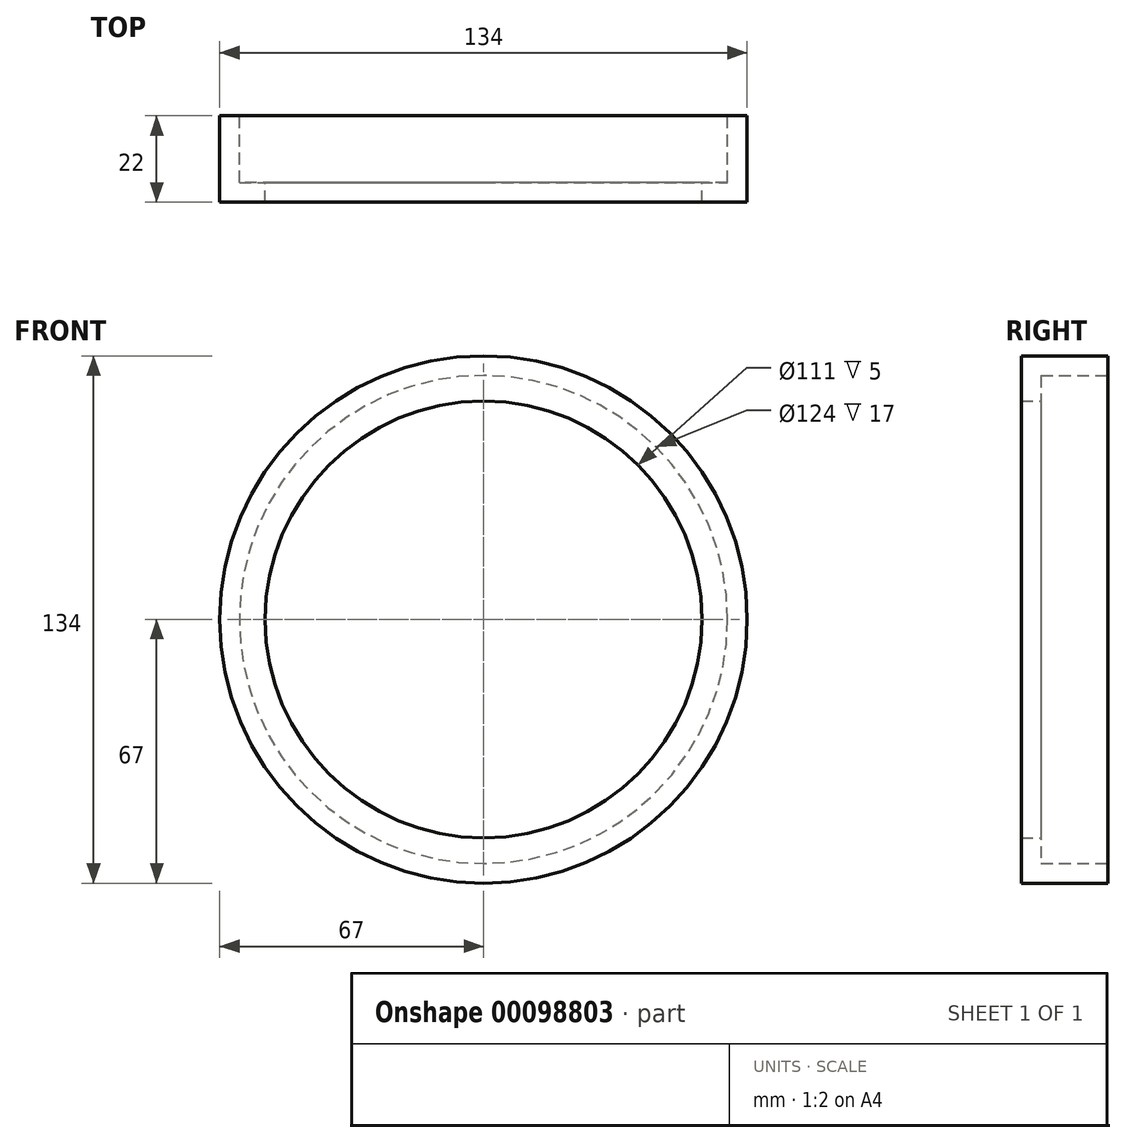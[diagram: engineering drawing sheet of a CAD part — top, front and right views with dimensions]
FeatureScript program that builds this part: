
annotation { "Feature Type Name" : "Feature", "Feature Type Description" : "" }
export const myFeature = defineFeature(function(context is Context, id is Id, definition is map)
    precondition{}
    {
        {
            var Q0;
            Q0=qCreatedBy(makeId("Top.planeOp"),FACE);
            var sketch = newSketch(context, id + "F0", { "sketchPlane" : qUnion([Q0])});
            skLineSegment(sketch, "E0", {"start": v(0, 100.09) * mm, "end": v(0, -91.13) * mm, "construction": true});
            skLineSegment(sketch, "E1", {"start": v(55.5, 0.07) * mm, "end": v(67, 0.07) * mm});
            skLineSegment(sketch, "E2", {"start": v(67, 0.07) * mm, "end": v(67, 22.07) * mm});
            skLineSegment(sketch, "E3", {"start": v(67, 22.07) * mm, "end": v(62, 22.07) * mm});
            skLineSegment(sketch, "E4", {"start": v(62, 22.07) * mm, "end": v(62, 5.07) * mm});
            skLineSegment(sketch, "E5", {"start": v(62, 5.07) * mm, "end": v(55.5, 5.07) * mm});
            skLineSegment(sketch, "E6", {"start": v(55.5, 5.07) * mm, "end": v(55.5, 0.07) * mm});
            skSolve(sketch);
        }
        {
            var Q0;
            Q0 = qSketchRegion(id + "F0", true);
            var Q1;
            Q1=sQuery(id+"F0.wireOp",EDGE,"E0");
            revolve(context, id + "F1", {"entities" : qUnion([Q0]), "axis" : qUnion([Q1]), "revolveType" : RevolveType.FULL});
        }
    });
